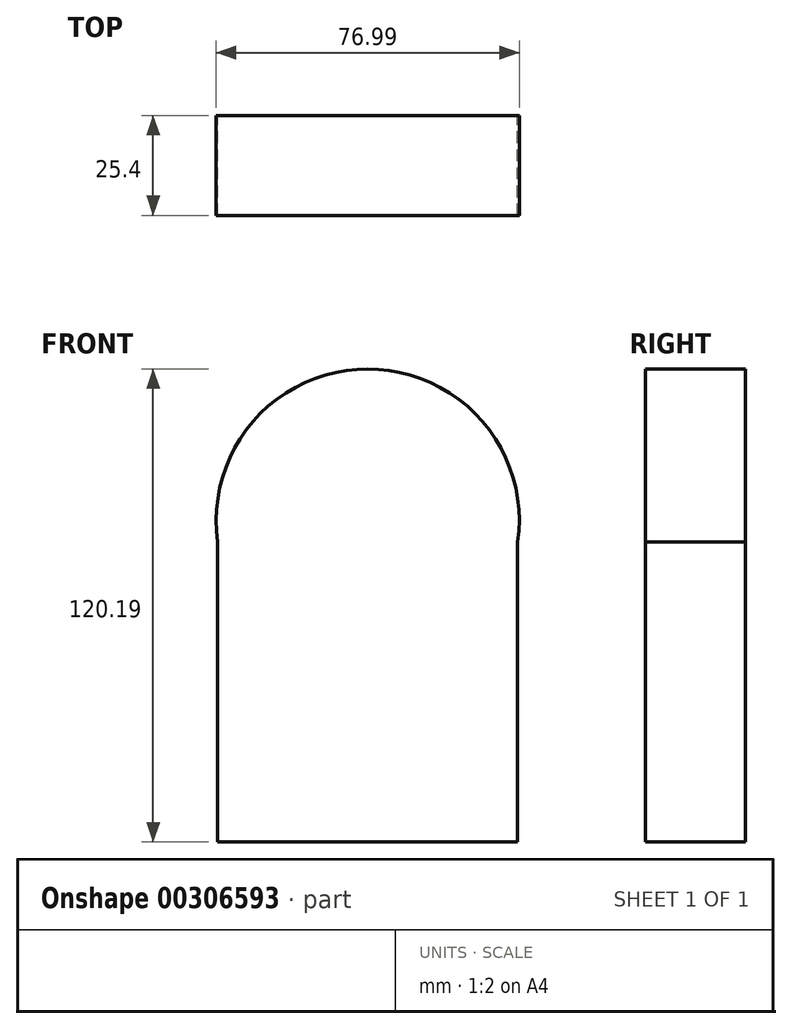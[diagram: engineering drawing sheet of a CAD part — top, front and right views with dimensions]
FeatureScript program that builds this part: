
annotation { "Feature Type Name" : "Feature", "Feature Type Description" : "" }
export const myFeature = defineFeature(function(context is Context, id is Id, definition is map)
    precondition{}
    {
        {
            var Q0;
            Q0=qCreatedBy(makeId("Front.planeOp"),FACE);
            var sketch = newSketch(context, id + "F0", { "sketchPlane" : qUnion([Q0])});
            skLineSegment(sketch, "E0", {"start": v(-40.3, 0) * mm, "end": v(-40.3, -76.2) * mm});
            skLineSegment(sketch, "E1", {"start": v(35.9, -76.2) * mm, "end": v(35.9, 0) * mm});
            skArc(sketch, "E2", {"start": v(35.9, 0) * mm, "mid": v(-2.2, 44) * mm, "end": v(-40.3, 0) * mm});
            skLineSegment(sketch, "E3", {"start": v(-40.3, -76.2) * mm, "end": v(35.9, -76.2) * mm});
            skSolve(sketch);
        }
        {
            var Q0;
            Q0=makeQuery(id+"F0.imprint","IMPRINT",FACE,{"disambiguationData":[TD([[makeQuery(id+"F0.imprint","IMPRINT",EDGE,{"derivedFrom":sQuery(id+"F0.wireOp",EDGE,"E0")}),1.0]])]});
            extrude(context, id + "F1", {"entities" : qUnion([Q0]), "depth" : 25.4 * mm});
        }
    });
